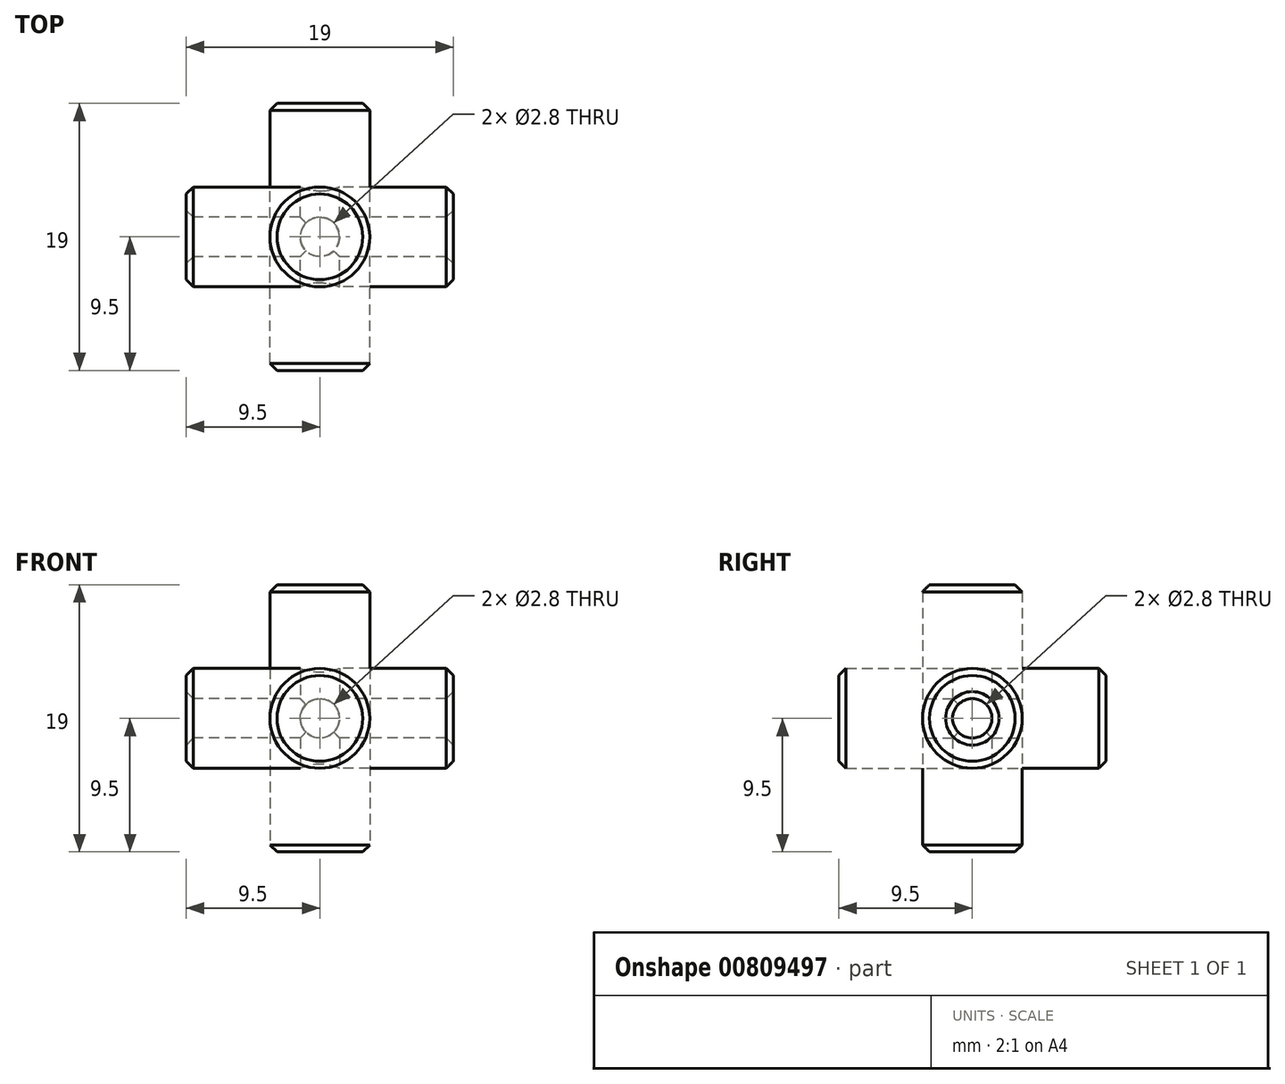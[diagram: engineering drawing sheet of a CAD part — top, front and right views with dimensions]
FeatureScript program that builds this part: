
annotation { "Feature Type Name" : "Feature", "Feature Type Description" : "" }
export const myFeature = defineFeature(function(context is Context, id is Id, definition is map)
    precondition{}
    {
        {
            var Q0;
            Q0=qCreatedBy(makeId("Front.planeOp"),FACE);
            var sketch = newSketch(context, id + "F0", { "sketchPlane" : qUnion([Q0])});
            skCircle(sketch, "E0", {"center": v(0, 0) * mm, "radius": 3.55 * mm});
            skSolve(sketch);
        }
        {
            var Q0;
            Q0=makeQuery(id+"F0.imprint","IMPRINT",FACE,{"disambiguationData":[TD([[makeQuery(id+"F0.imprint","IMPRINT",EDGE,{"derivedFrom":sQuery(id+"F0.wireOp",EDGE,"E0")}),1.0]])]});
            extrude(context, id + "F1", {"entities" : qUnion([Q0]), "endBound" : BoundingType.SYMMETRIC, "depth" : 19 * mm, "offsetDistance" : 25.4 * mm});
        }
        {
            var Q0;
            Q0=qCreatedBy(makeId("Front.planeOp"),FACE);
            var sketch = newSketch(context, id + "F2", { "sketchPlane" : qUnion([Q0])});
            skCircle(sketch, "E1", {"center": v(0, 0) * mm, "radius": 1.4 * mm});
            skSolve(sketch);
        }
        {
            var Q0;
            Q0 = qSketchRegion(id + "F2", true);
            extrude(context, id + "F3", {"entities" : qUnion([Q0]), "endBound" : BoundingType.SYMMETRIC, "depth" : 20 * mm, "offsetDistance" : 25.4 * mm});
        }
        {
            var Q0;
            Q0=qCreatedBy(makeId("Front.planeOp"),FACE);
            var sketch = newSketch(context, id + "F4", { "sketchPlane" : qUnion([Q0])});
            skLineSegment(sketch, "E2.bottom", {"start": v(0, 0) * mm, "end": v(10, 0) * mm});
            skLineSegment(sketch, "E2.top", {"start": v(0, 10) * mm, "end": v(10, 10) * mm});
            skLineSegment(sketch, "E2.left", {"start": v(0, 0) * mm, "end": v(0, 10) * mm});
            skLineSegment(sketch, "E2.right", {"start": v(10, 0) * mm, "end": v(10, 10) * mm});
            skSolve(sketch);
        }
        {
            var Q0;
            Q0=makeQuery(id+"F4.imprint","IMPRINT",FACE,{"disambiguationData":[TD([[makeQuery(id+"F4.imprint","IMPRINT",EDGE,{"derivedFrom":sQuery(id+"F4.wireOp",EDGE,"E2.bottom")}),1.0]])]});
            extrude(context, id + "F5", {"entities" : qUnion([Q0]), "depth" : 10 * mm, "offsetDistance" : 25.4 * mm});
        }
        {
            var Q0;
            Q0=qCreatedBy(makeId("Origin.pointOp"),VERTEX);
            var Q1;
            Q1=makeQuery(id+"F5.opExtrude","CAP_VERTEX",VERTEX,{"disambiguationData":[OSD([sQuery(id+"F4.wireOp",EDGE,"E2.top"),sQuery(id+"F4.wireOp",EDGE,"E2.right")])],"isStart":false});
            var Q2;
            Q2=makeQuery(id+"F5.opExtrude","CAP_VERTEX",VERTEX,{"disambiguationData":[OSD([sQuery(id+"F4.wireOp",EDGE,"E2.bottom"),sQuery(id+"F4.wireOp",EDGE,"E2.right")])],"isStart":false});
            cPlane(context, id + "F6", {"entities" : qUnion([Q0, Q1, Q2]), "cplaneType" : CPlaneType.THREE_POINT, "offset" : 25.4 * mm, "width" : 152.4 * mm, "height" : 152.4 * mm});
        }
        {
            var Q0;
            Q0=qCreatedBy(id+"F6.planeOp",FACE);
            var sketch = newSketch(context, id + "F7", { "sketchPlane" : qUnion([Q0])});
            skLineSegment(sketch, "E3", {"start": v(0, 0) * mm, "end": v(14.14, 10) * mm});
            skSolve(sketch);
        }
        {
            var Q0;
            Q0=makeQuery(id+"F5.opExtrude","SWEPT_BODY",BODY,{"disambiguationData":[OSD([sQuery(id+"F4.wireOp",EDGE,"E2.bottom"),sQuery(id+"F4.wireOp",EDGE,"E2.top"),sQuery(id+"F4.wireOp",EDGE,"E2.left"),sQuery(id+"F4.wireOp",EDGE,"E2.right")])]});
            deleteBodies(context, id + "F8", {"entities" : qUnion([Q0])});
        }
        {
            var Q0;
            Q0=makeQuery(id+"F1.opExtrude","SWEPT_BODY",BODY,{"disambiguationData":[OSD([sQuery(id+"F0.wireOp",EDGE,"E0")])]});
            var Q1;
            Q1=makeQuery(id+"F3.opExtrude","SWEPT_BODY",BODY,{"disambiguationData":[OSD([sQuery(id+"F2.wireOp",EDGE,"E1")])]});
            var Q2;
            Q2=sQuery(id+"F7.wireOp",EDGE,"E3");
            circularPattern(context, id + "F9", {"entities" : qUnion([Q0, Q1]), "axis" : qUnion([Q2]), "angle" : 360 * degree, "instanceCount" : 3, "equalSpace" : true});
        }
        {
            var Q0;
            Q0=makeQuery(id+"F9.opPattern","COPY",BODY,{"derivedFrom":makeQuery(id+"F3.opExtrude","SWEPT_BODY",BODY,{"disambiguationData":[OSD([sQuery(id+"F2.wireOp",EDGE,"E1")])]}),"instanceName":"1"});
            var Q1;
            Q1=makeQuery(id+"F3.opExtrude","SWEPT_BODY",BODY,{"disambiguationData":[OSD([sQuery(id+"F2.wireOp",EDGE,"E1")])]});
            var Q2;
            Q2=makeQuery(id+"F9.opPattern","COPY",BODY,{"derivedFrom":makeQuery(id+"F3.opExtrude","SWEPT_BODY",BODY,{"disambiguationData":[OSD([sQuery(id+"F2.wireOp",EDGE,"E1")])]}),"instanceName":"2"});
            var Q3;
            Q3=makeQuery(id+"F9.opPattern","COPY",BODY,{"derivedFrom":makeQuery(id+"F1.opExtrude","SWEPT_BODY",BODY,{"disambiguationData":[OSD([sQuery(id+"F0.wireOp",EDGE,"E0")])]}),"instanceName":"1"});
            booleanBodies(context, id + "F10", {"operationType" : BooleanOperationType.SUBTRACTION, "tools" : qUnion([Q0, Q1, Q2]), "targets" : qUnion([Q3])});
        }
        {
            var Q0;
            Q0=makeQuery(id+"F10.opBoolean","INTERSECT",EDGE,{"derivedFrom":[makeQuery(id+"F9.opPattern","COPY",FACE,{"derivedFrom":makeQuery(id+"F1.opExtrude","CAP_FACE",FACE,{"disambiguationData":[OSD([sQuery(id+"F0.wireOp",EDGE,"E0")])],"isStart":false}),"instanceName":"1"}),makeQuery(id+"F9.opPattern","COPY",FACE,{"derivedFrom":makeQuery(id+"F3.opExtrude","SWEPT_FACE",FACE,{"disambiguationData":[OSD([sQuery(id+"F2.wireOp",EDGE,"E1")])]}),"instanceName":"1"})]});
            var Q1;
            Q1=makeQuery(id+"F1.opExtrude","CAP_EDGE",EDGE,{"disambiguationData":[OSD([sQuery(id+"F0.wireOp",EDGE,"E0")])],"isStart":false});
            var Q2;
            Q2=makeQuery(id+"F10.opBoolean","INTERSECT",EDGE,{"derivedFrom":[makeQuery(id+"F1.opExtrude","CAP_FACE",FACE,{"disambiguationData":[OSD([sQuery(id+"F0.wireOp",EDGE,"E0")])],"isStart":false}),makeQuery(id+"F3.opExtrude","SWEPT_FACE",FACE,{"disambiguationData":[OSD([sQuery(id+"F2.wireOp",EDGE,"E1")])]})]});
            var Q3;
            Q3=makeQuery(id+"F9.opPattern","COPY",EDGE,{"derivedFrom":makeQuery(id+"F1.opExtrude","CAP_EDGE",EDGE,{"disambiguationData":[OSD([sQuery(id+"F0.wireOp",EDGE,"E0")])],"isStart":false}),"instanceName":"1"});
            var Q4;
            Q4=makeQuery(id+"F9.opPattern","COPY",EDGE,{"derivedFrom":makeQuery(id+"F1.opExtrude","CAP_EDGE",EDGE,{"disambiguationData":[OSD([sQuery(id+"F0.wireOp",EDGE,"E0")])],"isStart":true}),"instanceName":"2"});
            var Q5;
            Q5=makeQuery(id+"F10.opBoolean","INTERSECT",EDGE,{"derivedFrom":[makeQuery(id+"F9.opPattern","COPY",FACE,{"derivedFrom":makeQuery(id+"F1.opExtrude","CAP_FACE",FACE,{"disambiguationData":[OSD([sQuery(id+"F0.wireOp",EDGE,"E0")])],"isStart":true}),"instanceName":"2"}),makeQuery(id+"F9.opPattern","COPY",FACE,{"derivedFrom":makeQuery(id+"F3.opExtrude","SWEPT_FACE",FACE,{"disambiguationData":[OSD([sQuery(id+"F2.wireOp",EDGE,"E1")])]}),"instanceName":"2"})]});
            var Q6;
            Q6=makeQuery(id+"F9.opPattern","COPY",EDGE,{"derivedFrom":makeQuery(id+"F1.opExtrude","CAP_EDGE",EDGE,{"disambiguationData":[OSD([sQuery(id+"F0.wireOp",EDGE,"E0")])],"isStart":true}),"instanceName":"1"});
            var Q7;
            Q7=makeQuery(id+"F10.opBoolean","INTERSECT",EDGE,{"derivedFrom":[makeQuery(id+"F9.opPattern","COPY",FACE,{"derivedFrom":makeQuery(id+"F1.opExtrude","CAP_FACE",FACE,{"disambiguationData":[OSD([sQuery(id+"F0.wireOp",EDGE,"E0")])],"isStart":true}),"instanceName":"1"}),makeQuery(id+"F9.opPattern","COPY",FACE,{"derivedFrom":makeQuery(id+"F3.opExtrude","SWEPT_FACE",FACE,{"disambiguationData":[OSD([sQuery(id+"F2.wireOp",EDGE,"E1")])]}),"instanceName":"1"})]});
            var Q8;
            Q8=makeQuery(id+"F9.opPattern","COPY",EDGE,{"derivedFrom":makeQuery(id+"F1.opExtrude","CAP_EDGE",EDGE,{"disambiguationData":[OSD([sQuery(id+"F0.wireOp",EDGE,"E0")])],"isStart":false}),"instanceName":"2"});
            var Q9;
            Q9=makeQuery(id+"F10.opBoolean","INTERSECT",EDGE,{"derivedFrom":[makeQuery(id+"F9.opPattern","COPY",FACE,{"derivedFrom":makeQuery(id+"F1.opExtrude","CAP_FACE",FACE,{"disambiguationData":[OSD([sQuery(id+"F0.wireOp",EDGE,"E0")])],"isStart":false}),"instanceName":"2"}),makeQuery(id+"F9.opPattern","COPY",FACE,{"derivedFrom":makeQuery(id+"F3.opExtrude","SWEPT_FACE",FACE,{"disambiguationData":[OSD([sQuery(id+"F2.wireOp",EDGE,"E1")])]}),"instanceName":"2"})]});
            var Q10;
            Q10=makeQuery(id+"F1.opExtrude","CAP_EDGE",EDGE,{"disambiguationData":[OSD([sQuery(id+"F0.wireOp",EDGE,"E0")])],"isStart":true});
            var Q11;
            Q11=makeQuery(id+"F10.opBoolean","INTERSECT",EDGE,{"derivedFrom":[makeQuery(id+"F1.opExtrude","CAP_FACE",FACE,{"disambiguationData":[OSD([sQuery(id+"F0.wireOp",EDGE,"E0")])],"isStart":true}),makeQuery(id+"F3.opExtrude","SWEPT_FACE",FACE,{"disambiguationData":[OSD([sQuery(id+"F2.wireOp",EDGE,"E1")])]})]});
            chamfer(context, id + "F11", {"entities" : qUnion([Q0, Q1, Q2, Q3, Q4, Q5, Q6, Q7, Q8, Q9, Q10, Q11]), "width" : 0.5 * mm, "tangentPropagation" : true});
        }
    });
